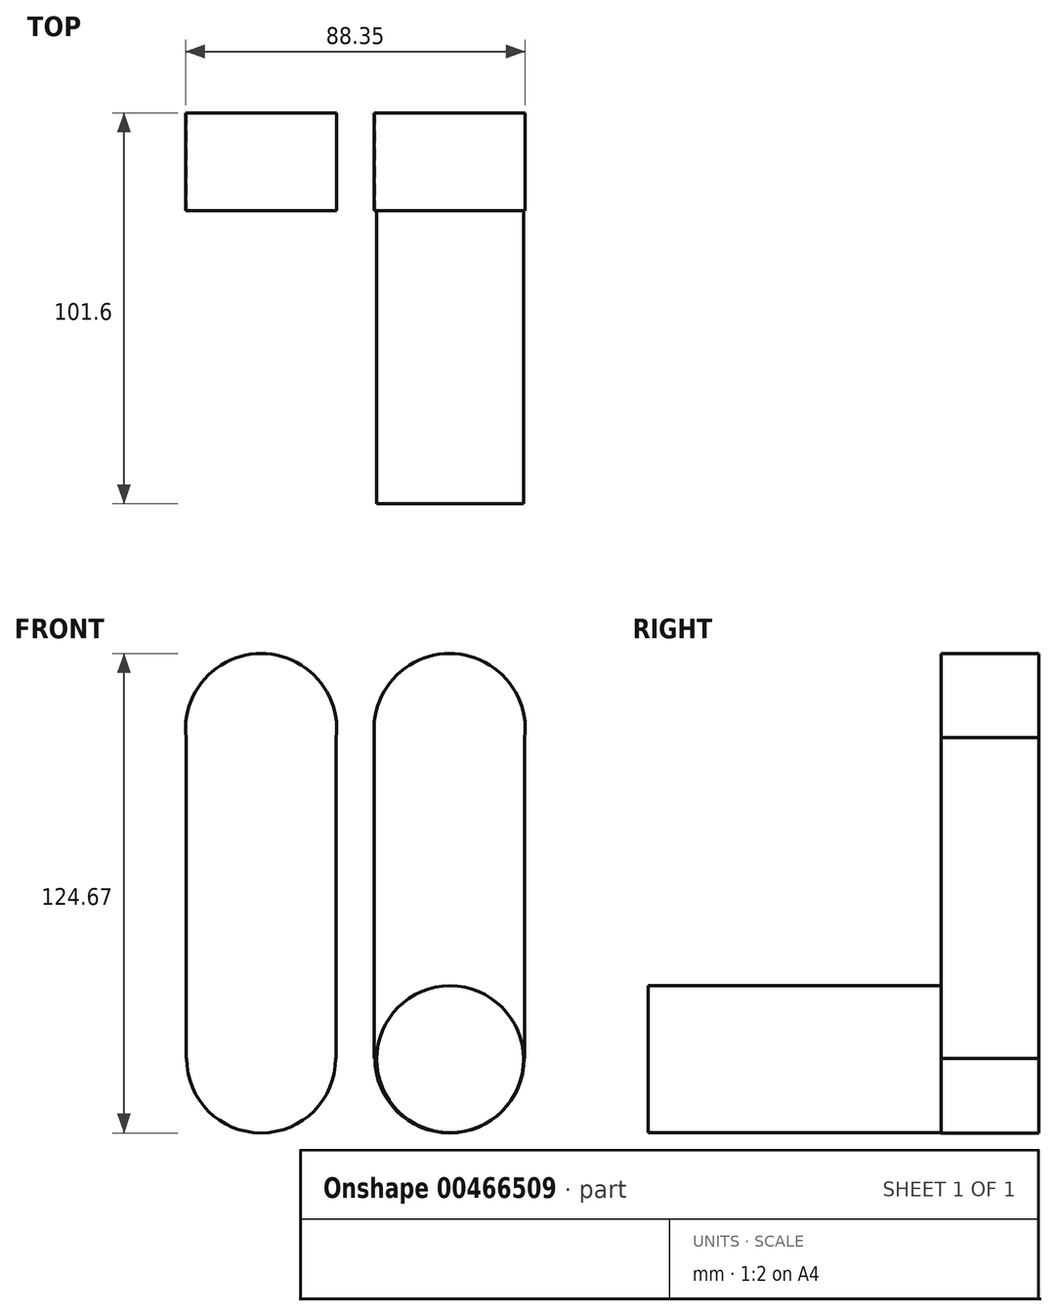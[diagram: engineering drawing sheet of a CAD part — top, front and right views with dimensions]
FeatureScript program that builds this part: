
annotation { "Feature Type Name" : "Feature", "Feature Type Description" : "" }
export const myFeature = defineFeature(function(context is Context, id is Id, definition is map)
    precondition{}
    {
        {
            var Q0;
            Q0=qCreatedBy(makeId("Front.planeOp"),FACE);
            var sketch = newSketch(context, id + "F0", { "sketchPlane" : qUnion([Q0])});
            skLineSegment(sketch, "E0.bottom", {"start": v(-19.55, 42.8) * mm, "end": v(19.55, 42.8) * mm});
            skLineSegment(sketch, "E0.top", {"start": v(-19.55, -42.8) * mm, "end": v(19.55, -42.8) * mm});
            skLineSegment(sketch, "E0.left", {"start": v(-19.55, 42.8) * mm, "end": v(-19.55, -42.8) * mm});
            skLineSegment(sketch, "E0.right", {"start": v(19.55, 42.8) * mm, "end": v(19.55, -42.8) * mm});
            skPoint(sketch, "E0.middle", {"position": v(0, 0) * mm});
            skCircle(sketch, "E1", {"center": v(0, 42.8) * mm, "radius": 19.67 * mm});
            skCircle(sketch, "E2", {"center": v(0, -42.8) * mm, "radius": 19.4 * mm});
            skSolve(sketch);
        }
        {
            var Q0;
            Q0 = qSketchRegion(id + "F0", true);
            extrude(context, id + "F1", {"entities" : qUnion([Q0]), "oppositeDirection" : true, "depth" : 25.4 * mm});
        }
        {
            var Q0;
            Q0=qCreatedBy(makeId("Front.planeOp"),FACE);
            var sketch = newSketch(context, id + "F2", { "sketchPlane" : qUnion([Q0])});
            skCircle(sketch, "E3", {"center": v(0.12, -43.02) * mm, "radius": 19.1 * mm});
            skPoint(sketch, "E3.first.point", {"position": v(-18.98, -42.76) * mm});
            skPoint(sketch, "E3.second.point", {"position": v(19.21, -43) * mm});
            skPoint(sketch, "E3.third.point", {"position": v(-4.45, -24.48) * mm});
            skSolve(sketch);
        }
        {
            var Q0;
            Q0 = qSketchRegion(id + "F2", true);
            extrude(context, id + "F3", {"entities" : qUnion([Q0]), "operationType" : NewBodyOperationType.ADD, "depth" : 76.2 * mm});
        }
        {
            var Q0;
            Q0=qCreatedBy(makeId("Front.planeOp"),FACE);
            var sketch = newSketch(context, id + "F4", { "sketchPlane" : qUnion([Q0])});
            skLineSegment(sketch, "E4.bottom", {"start": v(-68.57, 42.8) * mm, "end": v(-29.46, 42.8) * mm});
            skLineSegment(sketch, "E4.top", {"start": v(-68.57, -42.8) * mm, "end": v(-29.46, -42.8) * mm});
            skLineSegment(sketch, "E4.left", {"start": v(-68.57, 42.8) * mm, "end": v(-68.57, -42.8) * mm});
            skLineSegment(sketch, "E4.right", {"start": v(-29.46, 42.8) * mm, "end": v(-29.46, -42.8) * mm});
            skPoint(sketch, "E4.middle", {"position": v(-49.01, 0) * mm});
            skCircle(sketch, "E5", {"center": v(-49.01, 42.8) * mm, "radius": 19.67 * mm});
            skCircle(sketch, "E6", {"center": v(-49.01, -42.8) * mm, "radius": 19.4 * mm});
            skSolve(sketch);
        }
        {
            var Q0;
            Q0 = qSketchRegion(id + "F4", true);
            extrude(context, id + "F5", {"entities" : qUnion([Q0]), "oppositeDirection" : true, "depth" : 25.4 * mm});
        }
    });
